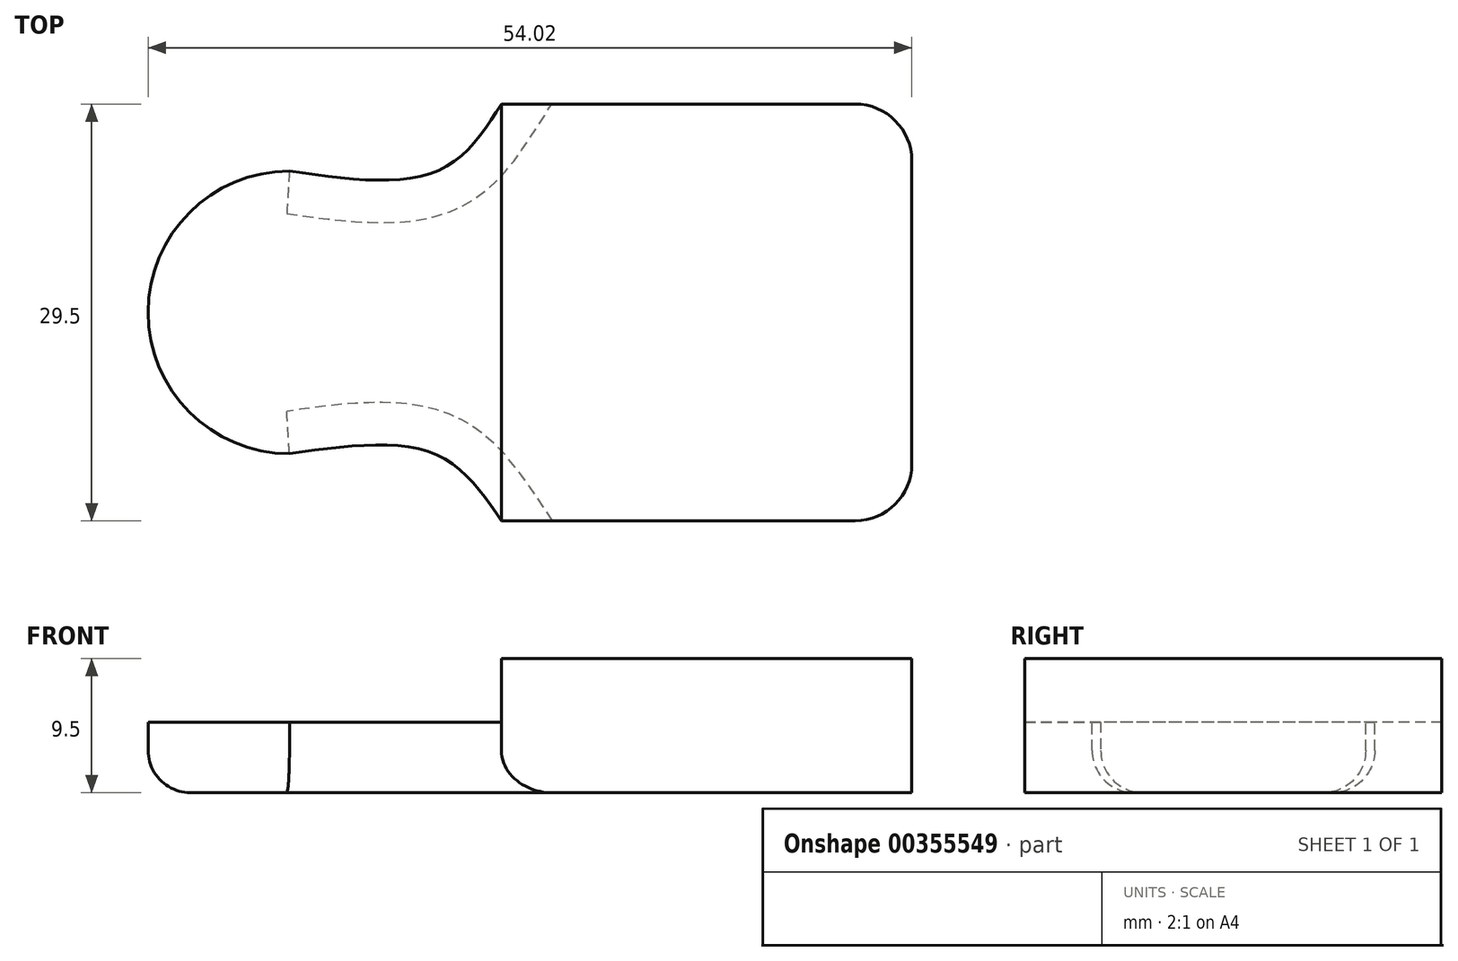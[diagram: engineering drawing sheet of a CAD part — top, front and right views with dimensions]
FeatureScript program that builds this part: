
annotation { "Feature Type Name" : "Feature", "Feature Type Description" : "" }
export const myFeature = defineFeature(function(context is Context, id is Id, definition is map)
    precondition{}
    {
        {
            var Q0;
            Q0=qCreatedBy(makeId("Top.planeOp"),FACE);
            var sketch = newSketch(context, id + "F0", { "sketchPlane" : qUnion([Q0])});
            skLineSegment(sketch, "E0.bottom", {"start": v(-3.84, 14.11) * mm, "end": v(21.18, 14.11) * mm});
            skLineSegment(sketch, "E0.top", {"start": v(-3.84, -15.39) * mm, "end": v(21.18, -15.39) * mm});
            skLineSegment(sketch, "E0.right", {"start": v(25.18, 10.11) * mm, "end": v(25.18, -11.39) * mm});
            skLineSegment(sketch, "E1", {"start": v(-3.84, 14.11) * mm, "end": v(-3.84, -15.39) * mm, "construction": true});
            skLineSegment(sketch, "E2", {"start": v(-28.84, 9.36) * mm, "end": v(-3.84, 9.36) * mm, "construction": true});
            skLineSegment(sketch, "E3", {"start": v(-28.84, -10.64) * mm, "end": v(-3.84, -10.64) * mm, "construction": true});
            skArc(sketch, "E4", {"start": v(-18.84, 9.36) * mm, "mid": v(-28.84, -0.64) * mm, "end": v(-18.84, -10.64) * mm});
            skPoint(sketch, "E4.first.point", {"position": v(-28.84, -0.64) * mm});
            skPoint(sketch, "E4.second.point", {"position": v(-8.84, -0.64) * mm});
            skPoint(sketch, "E4.second.point.positionSnap0", {"position": v(-28.84, -0.64) * mm});
            skPoint(sketch, "E4.third.point", {"position": v(-11.06, -6.92) * mm});
            skFitSpline(sketch, "E5", {"points": [v(-3.84, 14.11) * mm, v(-8.38, 9.36) * mm, v(-18.84, 9.36) * mm], "startDerivative": vector(-8.4, -13.12) * mm, "endDerivative": vector(-21.11, 3) * mm});
            skFitSpline(sketch, "E6", {"points": [v(-3.84, -15.39) * mm, v(-8.6, -10.64) * mm, v(-18.84, -10.64) * mm], "startDerivative": vector(-8.87, 12.99) * mm, "endDerivative": vector(-20.72, -2.93) * mm});
            skPoint(sketch, "E7.orphan", {"position": v(-28.84, 14.11) * mm});
            skPoint(sketch, "E8.orphan", {"position": v(-28.84, -15.39) * mm});
            skArc(sketch, "E9", {"start": v(25.18, 10.11) * mm, "mid": v(24, 12.94) * mm, "end": v(21.18, 14.11) * mm});
            skArc(sketch, "E10", {"start": v(21.18, -15.39) * mm, "mid": v(24, -14.21) * mm, "end": v(25.18, -11.39) * mm});
            skPoint(sketch, "E11.orphan", {"position": v(25.18, -15.39) * mm});
            skPoint(sketch, "E12.orphan", {"position": v(25.18, 14.11) * mm});
            skSolve(sketch);
        }
        {
            var Q0;
            Q0=makeQuery(id+"F0.imprint","IMPRINT",FACE,{"disambiguationData":[TD([[makeQuery(id+"F0.imprint","IMPRINT",EDGE,{"derivedFrom":sQuery(id+"F0.wireOp",EDGE,"E0.bottom")}),-1.0]])]});
            extrude(context, id + "F1", {"entities" : qUnion([Q0]), "oppositeDirection" : true, "depth" : 5 * mm});
        }
        {
            var Q0;
            Q0=makeQuery(id+"F1.opExtrude","CAP_FACE",FACE,{"disambiguationData":[OSD([sQuery(id+"F0.wireOp",EDGE,"E0.bottom"),sQuery(id+"F0.wireOp",EDGE,"E0.top"),sQuery(id+"F0.wireOp",EDGE,"E0.right"),sQuery(id+"F0.wireOp",EDGE,"E4"),sQuery(id+"F0.wireOp",EDGE,"E5"),sQuery(id+"F0.wireOp",EDGE,"E6"),sQuery(id+"F0.wireOp",EDGE,"E9"),sQuery(id+"F0.wireOp",EDGE,"E10")])],"isStart":true});
            var sketch = newSketch(context, id + "F2", { "sketchPlane" : qUnion([Q0])});
            skLineSegment(sketch, "E13.0.1", {"start": v(-3.84, -15.39) * mm, "end": v(21.18, -15.39) * mm});
            skArc(sketch, "E13.0.2", {"start": v(21.18, -15.39) * mm, "mid": v(24, -14.21) * mm, "end": v(25.18, -11.39) * mm});
            skLineSegment(sketch, "E13.0.3", {"start": v(25.18, -11.39) * mm, "end": v(25.18, 10.11) * mm});
            skArc(sketch, "E13.0.4", {"start": v(25.18, 10.11) * mm, "mid": v(24, 12.94) * mm, "end": v(21.18, 14.11) * mm});
            skLineSegment(sketch, "E13.0.5", {"start": v(21.18, 14.11) * mm, "end": v(-3.84, 14.11) * mm});
            skLineSegment(sketch, "E14", {"start": v(-3.84, 14.11) * mm, "end": v(-3.84, -15.39) * mm});
            skPoint(sketch, "E13.0.7.start.orphan", {"position": v(-18.84, 9.36) * mm});
            skPoint(sketch, "E13.0.0.start.orphan", {"position": v(-18.84, -10.64) * mm});
            skSolve(sketch);
        }
        {
            var Q0;
            Q0=makeQuery(id+"F2.imprint","IMPRINT",FACE,{"disambiguationData":[TD([[makeQuery(id+"F2.imprint","IMPRINT",EDGE,{"derivedFrom":sQuery(id+"F2.wireOp",EDGE,"E13.0.1")}),1.0]])]});
            extrude(context, id + "F3", {"entities" : qUnion([Q0]), "operationType" : NewBodyOperationType.ADD, "depth" : 4.5 * mm});
        }
        {
            var Q0;
            Q0=makeQuery(id+"F1.opExtrude","CAP_EDGE",EDGE,{"disambiguationData":[OSD([sQuery(id+"F0.wireOp",EDGE,"E5")])],"isStart":false});
            var Q1;
            Q1=makeQuery(id+"F1.opExtrude","CAP_EDGE",EDGE,{"disambiguationData":[OSD([sQuery(id+"F0.wireOp",EDGE,"E4")])],"isStart":false});
            var Q2;
            Q2=makeQuery(id+"F1.opExtrude","CAP_EDGE",EDGE,{"disambiguationData":[OSD([sQuery(id+"F0.wireOp",EDGE,"E6")])],"isStart":false});
            fillet(context, id + "F4", {"entities" : qUnion([Q0, Q1, Q2]), "radius" : 3 * mm, "tangentPropagation" : true, "allowEdgeOverflow" : false});
        }
    });
